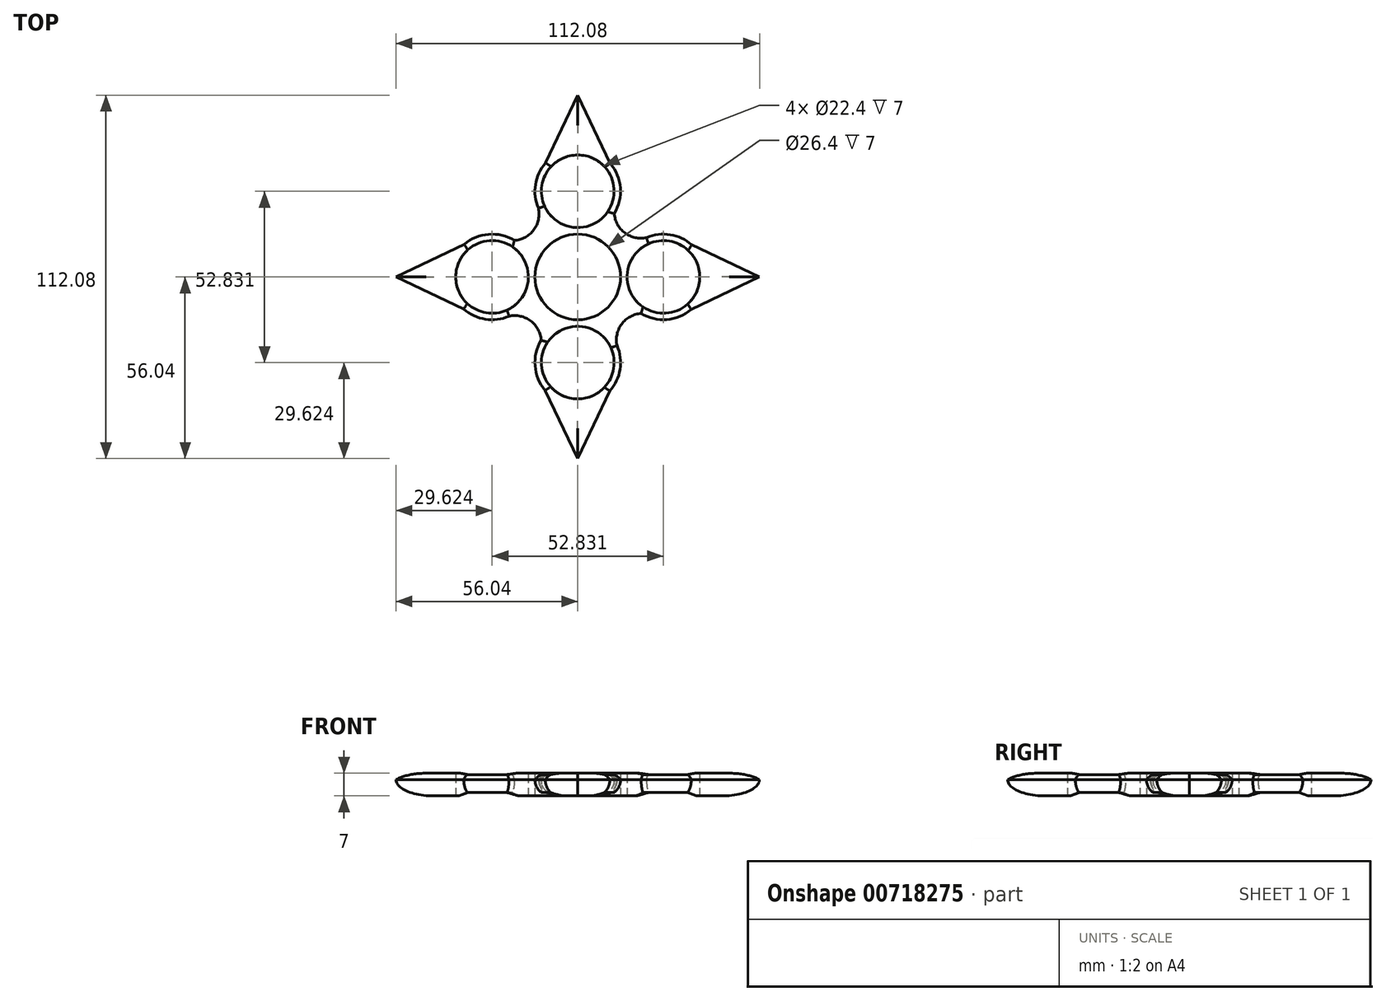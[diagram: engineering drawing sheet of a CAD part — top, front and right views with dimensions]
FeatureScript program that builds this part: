
annotation { "Feature Type Name" : "Feature", "Feature Type Description" : "" }
export const myFeature = defineFeature(function(context is Context, id is Id, definition is map)
    precondition{}
    {
        {
            var Q0;
            Q0=qCreatedBy(makeId("Top.planeOp"),FACE);
            var sketch = newSketch(context, id + "F0", { "sketchPlane" : qUnion([Q0])});
            skCircle(sketch, "E0", {"center": v(0, 0) * mm, "radius": 11.2 * mm});
            skCircle(sketch, "E1", {"center": v(0, 0) * mm, "radius": 13.2 * mm});
            skCircle(sketch, "E2", {"center": v(0, 26.42) * mm, "radius": 11.2 * mm});
            skArc(sketch, "E3", {"start": v(11.27, 19.54) * mm, "mid": v(0.92, 39.58) * mm, "end": v(-12.12, 21.18) * mm});
            skArc(sketch, "E4.1.0", {"start": v(-19.54, 11.27) * mm, "mid": v(-39.58, 0.92) * mm, "end": v(-21.18, -12.12) * mm});
            skCircle(sketch, "E4.1.1", {"center": v(-26.42, 0) * mm, "radius": 11.2 * mm});
            skArc(sketch, "E4.2.0", {"start": v(-11.27, -19.54) * mm, "mid": v(-0.92, -39.58) * mm, "end": v(12.12, -21.18) * mm});
            skCircle(sketch, "E4.2.1", {"center": v(0, -26.42) * mm, "radius": 11.2 * mm});
            skArc(sketch, "E4.3.0", {"start": v(19.54, -11.27) * mm, "mid": v(39.58, -0.92) * mm, "end": v(21.18, 12.12) * mm});
            skCircle(sketch, "E4.3.1", {"center": v(26.42, 0) * mm, "radius": 11.2 * mm});
            skLineSegment(sketch, "E5", {"start": v(-9.89, 35.16) * mm, "end": v(0, 56.04) * mm});
            skLineSegment(sketch, "E6", {"start": v(0, 56.04) * mm, "end": v(10.04, 35) * mm});
            skLineSegment(sketch, "E7.1.0", {"start": v(-35.16, -9.89) * mm, "end": v(-56.04, 0) * mm});
            skLineSegment(sketch, "E7.1.1", {"start": v(-56.04, 0) * mm, "end": v(-35, 10.04) * mm});
            skLineSegment(sketch, "E7.2.0", {"start": v(9.89, -35.16) * mm, "end": v(0, -56.04) * mm});
            skLineSegment(sketch, "E7.2.1", {"start": v(0, -56.04) * mm, "end": v(-10.04, -35) * mm});
            skLineSegment(sketch, "E7.3.0", {"start": v(35.16, 9.89) * mm, "end": v(56.04, 0) * mm});
            skLineSegment(sketch, "E7.3.1", {"start": v(56.04, 0) * mm, "end": v(35, -10.04) * mm});
            skArc(sketch, "E8", {"start": v(-19.54, 11.27) * mm, "mid": v(-13.56, 14.53) * mm, "end": v(-12.12, 21.18) * mm});
            skArc(sketch, "E9.1.0", {"start": v(-11.27, -19.54) * mm, "mid": v(-14.53, -13.56) * mm, "end": v(-21.18, -12.12) * mm});
            skArc(sketch, "E9.2.0", {"start": v(19.54, -11.27) * mm, "mid": v(13.56, -14.53) * mm, "end": v(12.12, -21.18) * mm});
            skArc(sketch, "E9.3.0", {"start": v(11.27, 19.54) * mm, "mid": v(14.53, 13.56) * mm, "end": v(21.18, 12.12) * mm});
            skSolve(sketch);
        }
        {
            var Q0;
            Q0=makeQuery(id+"F0.imprint","IMPRINT",FACE,{"disambiguationData":[TD([[makeQuery(id+"F0.imprint","IMPRINT",EDGE,{"derivedFrom":sQuery(id+"F0.wireOp",EDGE,"E1")}),-1.0]])]});
            var Q1;
            {var subQ0=sQuery(id+"F0.wireOp",EDGE,"E7.2.0");Q1=makeQuery(id+"F0.imprint","IMPRINT",FACE,{"disambiguationData":[TD([[makeQuery(id+"F0.imprint","IMPRINT",EDGE,{"derivedFrom":subQ0}),-1.0]])]});}
            var Q2;
            {var subQ0=sQuery(id+"F0.wireOp",EDGE,"E7.3.0");Q2=makeQuery(id+"F0.imprint","IMPRINT",FACE,{"disambiguationData":[TD([[makeQuery(id+"F0.imprint","IMPRINT",EDGE,{"derivedFrom":subQ0}),-1.0]])]});}
            var Q3;
            {var subQ0=sQuery(id+"F0.wireOp",EDGE,"E7.1.0");Q3=makeQuery(id+"F0.imprint","IMPRINT",FACE,{"disambiguationData":[TD([[makeQuery(id+"F0.imprint","IMPRINT",EDGE,{"derivedFrom":subQ0}),-1.0]])]});}
            var Q4;
            {var subQ0=sQuery(id+"F0.wireOp",EDGE,"E5");Q4=makeQuery(id+"F0.imprint","IMPRINT",FACE,{"disambiguationData":[TD([[makeQuery(id+"F0.imprint","IMPRINT",EDGE,{"derivedFrom":subQ0}),-1.0]])]});}
            extrude(context, id + "F1", {"entities" : qUnion([Q0, Q1, Q2, Q3, Q4]), "depth" : 7 * mm, "offsetDistance" : 25 * mm});
        }
        {
            var Q0;
            {var subQ0=sQuery(id+"F0.wireOp",EDGE,"E4.2.0");Q0=makeQuery(id+"F1.opExtrude","CAP_EDGE",EDGE,{"disambiguationData":[OSD([subQ0]),TDD([makeQuery(id+"F0.imprint","IMPRINT",EDGE,{"disambiguationData":[TD([[makeQuery(id+"F0.imprint","INTERSECT",VERTEX,{"derivedFrom":[subQ0,sQuery(id+"F0.wireOp",EDGE,"E9.1.0")]}),-1.0]])],"derivedFrom":subQ0})])],"isStart":true});}
            var Q1;
            Q1=makeQuery(id+"F1.opExtrude","CAP_EDGE",EDGE,{"disambiguationData":[OSD([sQuery(id+"F0.wireOp",EDGE,"E7.2.1")])],"isStart":true});
            var Q2;
            Q2=makeQuery(id+"F1.opExtrude","CAP_EDGE",EDGE,{"disambiguationData":[OSD([sQuery(id+"F0.wireOp",EDGE,"E7.2.0")])],"isStart":true});
            var Q3;
            {var subQ0=sQuery(id+"F0.wireOp",EDGE,"E4.2.0");Q3=makeQuery(id+"F1.opExtrude","CAP_EDGE",EDGE,{"disambiguationData":[OSD([subQ0]),TDD([makeQuery(id+"F0.imprint","IMPRINT",EDGE,{"disambiguationData":[TD([[makeQuery(id+"F0.imprint","INTERSECT",VERTEX,{"derivedFrom":[subQ0,sQuery(id+"F0.wireOp",EDGE,"E9.2.0")]}),1.0]])],"derivedFrom":subQ0})])],"isStart":true});}
            var Q4;
            Q4=makeQuery(id+"F1.opExtrude","CAP_EDGE",EDGE,{"disambiguationData":[OSD([sQuery(id+"F0.wireOp",EDGE,"E9.2.0")])],"isStart":true});
            var Q5;
            {var subQ0=sQuery(id+"F0.wireOp",EDGE,"E4.3.0");Q5=makeQuery(id+"F1.opExtrude","CAP_EDGE",EDGE,{"disambiguationData":[OSD([subQ0]),TDD([makeQuery(id+"F0.imprint","IMPRINT",EDGE,{"disambiguationData":[TD([[makeQuery(id+"F0.imprint","INTERSECT",VERTEX,{"derivedFrom":[subQ0,sQuery(id+"F0.wireOp",EDGE,"E9.2.0")]}),-1.0]])],"derivedFrom":subQ0})])],"isStart":true});}
            var Q6;
            Q6=makeQuery(id+"F1.opExtrude","CAP_EDGE",EDGE,{"disambiguationData":[OSD([sQuery(id+"F0.wireOp",EDGE,"E7.3.1")])],"isStart":true});
            var Q7;
            Q7=makeQuery(id+"F1.opExtrude","CAP_EDGE",EDGE,{"disambiguationData":[OSD([sQuery(id+"F0.wireOp",EDGE,"E7.3.0")])],"isStart":true});
            var Q8;
            {var subQ0=sQuery(id+"F0.wireOp",EDGE,"E4.3.0");Q8=makeQuery(id+"F1.opExtrude","CAP_EDGE",EDGE,{"disambiguationData":[OSD([subQ0]),TDD([makeQuery(id+"F0.imprint","IMPRINT",EDGE,{"disambiguationData":[TD([[makeQuery(id+"F0.imprint","INTERSECT",VERTEX,{"derivedFrom":[subQ0,sQuery(id+"F0.wireOp",EDGE,"E9.3.0")]}),1.0]])],"derivedFrom":subQ0})])],"isStart":true});}
            var Q9;
            Q9=makeQuery(id+"F1.opExtrude","CAP_EDGE",EDGE,{"disambiguationData":[OSD([sQuery(id+"F0.wireOp",EDGE,"E9.3.0")])],"isStart":true});
            var Q10;
            {var subQ0=sQuery(id+"F0.wireOp",EDGE,"E3");Q10=makeQuery(id+"F1.opExtrude","CAP_EDGE",EDGE,{"disambiguationData":[OSD([subQ0]),TDD([makeQuery(id+"F0.imprint","IMPRINT",EDGE,{"disambiguationData":[TD([[makeQuery(id+"F0.imprint","INTERSECT",VERTEX,{"derivedFrom":[subQ0,sQuery(id+"F0.wireOp",EDGE,"E9.3.0")]}),-1.0]])],"derivedFrom":subQ0})])],"isStart":true});}
            var Q11;
            Q11=makeQuery(id+"F1.opExtrude","CAP_EDGE",EDGE,{"disambiguationData":[OSD([sQuery(id+"F0.wireOp",EDGE,"E6")])],"isStart":true});
            var Q12;
            Q12=makeQuery(id+"F1.opExtrude","CAP_EDGE",EDGE,{"disambiguationData":[OSD([sQuery(id+"F0.wireOp",EDGE,"E5")])],"isStart":true});
            var Q13;
            {var subQ0=sQuery(id+"F0.wireOp",EDGE,"E3");Q13=makeQuery(id+"F1.opExtrude","CAP_EDGE",EDGE,{"disambiguationData":[OSD([subQ0]),TDD([makeQuery(id+"F0.imprint","IMPRINT",EDGE,{"disambiguationData":[TD([[makeQuery(id+"F0.imprint","INTERSECT",VERTEX,{"derivedFrom":[subQ0,sQuery(id+"F0.wireOp",EDGE,"E8")]}),1.0]])],"derivedFrom":subQ0})])],"isStart":true});}
            var Q14;
            Q14=makeQuery(id+"F1.opExtrude","CAP_EDGE",EDGE,{"disambiguationData":[OSD([sQuery(id+"F0.wireOp",EDGE,"E8")])],"isStart":true});
            var Q15;
            {var subQ0=sQuery(id+"F0.wireOp",EDGE,"E4.1.0");Q15=makeQuery(id+"F1.opExtrude","CAP_EDGE",EDGE,{"disambiguationData":[OSD([subQ0]),TDD([makeQuery(id+"F0.imprint","IMPRINT",EDGE,{"disambiguationData":[TD([[makeQuery(id+"F0.imprint","INTERSECT",VERTEX,{"derivedFrom":[subQ0,sQuery(id+"F0.wireOp",EDGE,"E8")]}),-1.0]])],"derivedFrom":subQ0})])],"isStart":true});}
            var Q16;
            Q16=makeQuery(id+"F1.opExtrude","CAP_EDGE",EDGE,{"disambiguationData":[OSD([sQuery(id+"F0.wireOp",EDGE,"E7.1.1")])],"isStart":true});
            var Q17;
            Q17=makeQuery(id+"F1.opExtrude","CAP_EDGE",EDGE,{"disambiguationData":[OSD([sQuery(id+"F0.wireOp",EDGE,"E7.1.0")])],"isStart":true});
            var Q18;
            {var subQ0=sQuery(id+"F0.wireOp",EDGE,"E4.1.0");Q18=makeQuery(id+"F1.opExtrude","CAP_EDGE",EDGE,{"disambiguationData":[OSD([subQ0]),TDD([makeQuery(id+"F0.imprint","IMPRINT",EDGE,{"disambiguationData":[TD([[makeQuery(id+"F0.imprint","INTERSECT",VERTEX,{"derivedFrom":[subQ0,sQuery(id+"F0.wireOp",EDGE,"E9.1.0")]}),1.0]])],"derivedFrom":subQ0})])],"isStart":true});}
            var Q19;
            Q19=makeQuery(id+"F1.opExtrude","CAP_EDGE",EDGE,{"disambiguationData":[OSD([sQuery(id+"F0.wireOp",EDGE,"E9.1.0")])],"isStart":true});
            fillet(context, id + "F2", {"entities" : qUnion([Q0, Q1, Q2, Q3, Q4, Q5, Q6, Q7, Q8, Q9, Q10, Q11, Q12, Q13, Q14, Q15, Q16, Q17, Q18, Q19]), "radius" : 5 * mm, "tangentPropagation" : true, "allowEdgeOverflow" : false});
        }
        {
            var Q0;
            Q0=makeQuery(id+"F1.opExtrude","CAP_EDGE",EDGE,{"disambiguationData":[OSD([sQuery(id+"F0.wireOp",EDGE,"E7.3.1")])],"isStart":false});
            var Q1;
            Q1=makeQuery(id+"F1.opExtrude","CAP_EDGE",EDGE,{"disambiguationData":[OSD([sQuery(id+"F0.wireOp",EDGE,"E7.3.0")])],"isStart":false});
            var Q2;
            Q2=makeQuery(id+"F1.opExtrude","CAP_EDGE",EDGE,{"disambiguationData":[OSD([sQuery(id+"F0.wireOp",EDGE,"E7.2.0")])],"isStart":false});
            var Q3;
            Q3=makeQuery(id+"F1.opExtrude","CAP_EDGE",EDGE,{"disambiguationData":[OSD([sQuery(id+"F0.wireOp",EDGE,"E7.2.1")])],"isStart":false});
            fillet(context, id + "F3", {"entities" : qUnion([Q0, Q1, Q2, Q3]), "radius" : 5 * mm, "tangentPropagation" : true, "allowEdgeOverflow" : false});
        }
        {
            var Q0;
            Q0=makeQuery(id+"F1.opExtrude","CAP_EDGE",EDGE,{"disambiguationData":[OSD([sQuery(id+"F0.wireOp",EDGE,"E7.1.0")])],"isStart":false});
            var Q1;
            Q1=makeQuery(id+"F1.opExtrude","CAP_EDGE",EDGE,{"disambiguationData":[OSD([sQuery(id+"F0.wireOp",EDGE,"E7.1.1")])],"isStart":false});
            var Q2;
            Q2=makeQuery(id+"F1.opExtrude","CAP_EDGE",EDGE,{"disambiguationData":[OSD([sQuery(id+"F0.wireOp",EDGE,"E5")])],"isStart":false});
            var Q3;
            Q3=makeQuery(id+"F1.opExtrude","CAP_EDGE",EDGE,{"disambiguationData":[OSD([sQuery(id+"F0.wireOp",EDGE,"E6")])],"isStart":false});
            var Q4;
            Q4=makeQuery(id+"F1.opExtrude","CAP_EDGE",EDGE,{"disambiguationData":[OSD([sQuery(id+"F0.wireOp",EDGE,"E9.3.0")])],"isStart":false});
            var Q5;
            Q5=makeQuery(id+"F1.opExtrude","CAP_EDGE",EDGE,{"disambiguationData":[OSD([sQuery(id+"F0.wireOp",EDGE,"E8")])],"isStart":false});
            var Q6;
            Q6=makeQuery(id+"F1.opExtrude","CAP_EDGE",EDGE,{"disambiguationData":[OSD([sQuery(id+"F0.wireOp",EDGE,"E9.1.0")])],"isStart":false});
            var Q7;
            Q7=makeQuery(id+"F1.opExtrude","CAP_EDGE",EDGE,{"disambiguationData":[OSD([sQuery(id+"F0.wireOp",EDGE,"E9.2.0")])],"isStart":false});
            fillet(context, id + "F4", {"entities" : qUnion([Q0, Q1, Q2, Q3, Q4, Q5, Q6, Q7]), "radius" : 5 * mm, "tangentPropagation" : true, "allowEdgeOverflow" : false});
        }
        {
            var Q0;
            {var subQ0=sQuery(id+"F0.wireOp",EDGE,"E4.3.0");Q0=makeQuery(id+"F1.opExtrude","CAP_EDGE",EDGE,{"disambiguationData":[OSD([subQ0]),TDD([makeQuery(id+"F0.imprint","IMPRINT",EDGE,{"disambiguationData":[TD([[makeQuery(id+"F0.imprint","INTERSECT",VERTEX,{"derivedFrom":[subQ0,sQuery(id+"F0.wireOp",EDGE,"E9.2.0")]}),-1.0]])],"derivedFrom":subQ0})])],"isStart":false});}
            var Q1;
            {var subQ0=sQuery(id+"F0.wireOp",EDGE,"E4.3.0");Q1=makeQuery(id+"F1.opExtrude","CAP_EDGE",EDGE,{"disambiguationData":[OSD([subQ0]),TDD([makeQuery(id+"F0.imprint","IMPRINT",EDGE,{"disambiguationData":[TD([[makeQuery(id+"F0.imprint","INTERSECT",VERTEX,{"derivedFrom":[subQ0,sQuery(id+"F0.wireOp",EDGE,"E9.3.0")]}),1.0]])],"derivedFrom":subQ0})])],"isStart":false});}
            var Q2;
            {var subQ0=sQuery(id+"F0.wireOp",EDGE,"E4.1.0");Q2=makeQuery(id+"F1.opExtrude","CAP_EDGE",EDGE,{"disambiguationData":[OSD([subQ0]),TDD([makeQuery(id+"F0.imprint","IMPRINT",EDGE,{"disambiguationData":[TD([[makeQuery(id+"F0.imprint","INTERSECT",VERTEX,{"derivedFrom":[subQ0,sQuery(id+"F0.wireOp",EDGE,"E8")]}),-1.0]])],"derivedFrom":subQ0})])],"isStart":false});}
            var Q3;
            {var subQ0=sQuery(id+"F0.wireOp",EDGE,"E4.1.0");Q3=makeQuery(id+"F1.opExtrude","CAP_EDGE",EDGE,{"disambiguationData":[OSD([subQ0]),TDD([makeQuery(id+"F0.imprint","IMPRINT",EDGE,{"disambiguationData":[TD([[makeQuery(id+"F0.imprint","INTERSECT",VERTEX,{"derivedFrom":[subQ0,sQuery(id+"F0.wireOp",EDGE,"E9.1.0")]}),1.0]])],"derivedFrom":subQ0})])],"isStart":false});}
            var Q4;
            {var subQ0=sQuery(id+"F0.wireOp",EDGE,"E4.2.0");Q4=makeQuery(id+"F1.opExtrude","CAP_EDGE",EDGE,{"disambiguationData":[OSD([subQ0]),TDD([makeQuery(id+"F0.imprint","IMPRINT",EDGE,{"disambiguationData":[TD([[makeQuery(id+"F0.imprint","INTERSECT",VERTEX,{"derivedFrom":[subQ0,sQuery(id+"F0.wireOp",EDGE,"E9.1.0")]}),-1.0]])],"derivedFrom":subQ0})])],"isStart":false});}
            var Q5;
            {var subQ0=sQuery(id+"F0.wireOp",EDGE,"E4.2.0");Q5=makeQuery(id+"F1.opExtrude","CAP_EDGE",EDGE,{"disambiguationData":[OSD([subQ0]),TDD([makeQuery(id+"F0.imprint","IMPRINT",EDGE,{"disambiguationData":[TD([[makeQuery(id+"F0.imprint","INTERSECT",VERTEX,{"derivedFrom":[subQ0,sQuery(id+"F0.wireOp",EDGE,"E9.2.0")]}),1.0]])],"derivedFrom":subQ0})])],"isStart":false});}
            var Q6;
            {var subQ0=sQuery(id+"F0.wireOp",EDGE,"E3");Q6=makeQuery(id+"F1.opExtrude","CAP_EDGE",EDGE,{"disambiguationData":[OSD([subQ0]),TDD([makeQuery(id+"F0.imprint","IMPRINT",EDGE,{"disambiguationData":[TD([[makeQuery(id+"F0.imprint","INTERSECT",VERTEX,{"derivedFrom":[subQ0,sQuery(id+"F0.wireOp",EDGE,"E8")]}),1.0]])],"derivedFrom":subQ0})])],"isStart":false});}
            var Q7;
            {var subQ0=sQuery(id+"F0.wireOp",EDGE,"E3");Q7=makeQuery(id+"F1.opExtrude","CAP_EDGE",EDGE,{"disambiguationData":[OSD([subQ0]),TDD([makeQuery(id+"F0.imprint","IMPRINT",EDGE,{"disambiguationData":[TD([[makeQuery(id+"F0.imprint","INTERSECT",VERTEX,{"derivedFrom":[subQ0,sQuery(id+"F0.wireOp",EDGE,"E9.3.0")]}),-1.0]])],"derivedFrom":subQ0})])],"isStart":false});}
            fillet(context, id + "F5", {"entities" : qUnion([Q0, Q1, Q2, Q3, Q4, Q5, Q6, Q7]), "radius" : 5 * mm, "tangentPropagation" : true, "allowEdgeOverflow" : false});
        }
    });
